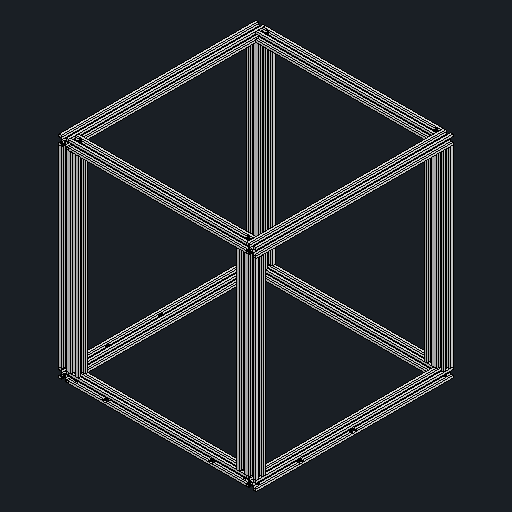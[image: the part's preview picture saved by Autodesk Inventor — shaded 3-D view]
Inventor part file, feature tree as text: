
AUTODESK INVENTOR PART (.ipt)
format: ipt  version: 2024.2 (Build 282272000, 272)  size: 997,376 bytes
history: native  units: mm
features: other x16, mirror x8
ambient origin geometry x8: Origin, YZ Plane, XZ Plane, XY Plane, X Axis, Y Axis, Z Axis, Center Point
bodies: Body1 (feature_tree), Body2 (feature_tree), Body3 (feature_tree), Body4 (feature_tree), Body5 (feature_tree), Body6 (feature_tree), Body7 (feature_tree), Body8 (feature_tree), Body9 (feature_tree), Body10 (feature_tree), Body11 (feature_tree), Body12 (feature_tree)
feature tree (24):
  other  "솔리드1"
  other  "솔리드2"
  other  "솔리드3"
  other  "솔리드4"
  other  "솔리드5"
  other  "솔리드6"
  other  "솔리드7"
  other  "솔리드8"
  other  "솔리드9"
  other  "솔리드10"
  other  "솔리드11"
  other  "솔리드12"
  other  "CBORE for M5 Hex Head Bolt2-mainborad[1]"
  other  "M5x0.8 Tapped Hole4-corner-pulleys[1]"
  other  "M5x0.8 Tapped Hole4-corner-pulleys[2]"
  mirror  "Mirror26-corner-pulleys[1]"
  other  "M5x0.8 Tapped Hole5-corner-brackets[1]"
  mirror  "Mirror27-corner-brackets[1]"
  mirror  "Mirror27-corner-brackets[2]"
  mirror  "Mirror28-corner-brackets[1]"
  mirror  "Mirror30-corner-brackets[1]"
  mirror  "Mirror30-corner-brackets[2]"
  mirror  "Mirror30-corner-brackets[3]"
  mirror  "Mirror26-corner-pulleys[3]"
